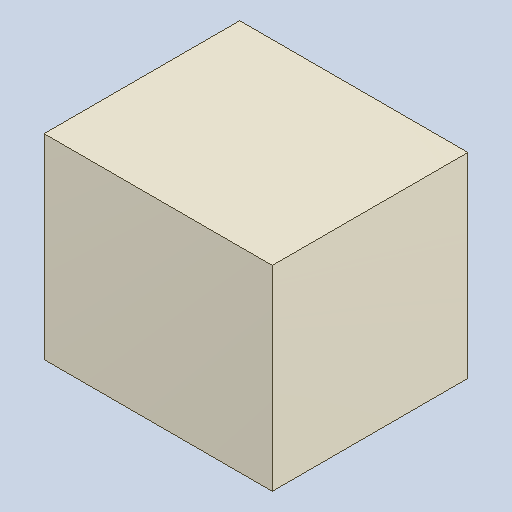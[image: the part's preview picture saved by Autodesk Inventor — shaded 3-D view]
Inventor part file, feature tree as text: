
AUTODESK INVENTOR PART (.ipt)
format: ipt  version: 2023.4 (Build 274418000, 418)  size: 82,432 bytes
history: native  units: mm
features: extrude x1
ambient origin geometry x8: Origin, YZ Plane, XZ Plane, XY Plane, X Axis, Y Axis, Z Axis, Center Point
bodies: Solid1 (feature_tree)
feature tree (1):
  extrude  "Extruded_4"  [1 undecoded]
note: 1 required parameter value undecoded (feature->parameter linkage not recoverable at this tier; creation-order binding heuristic only, values carry confidence <= 0.55)
